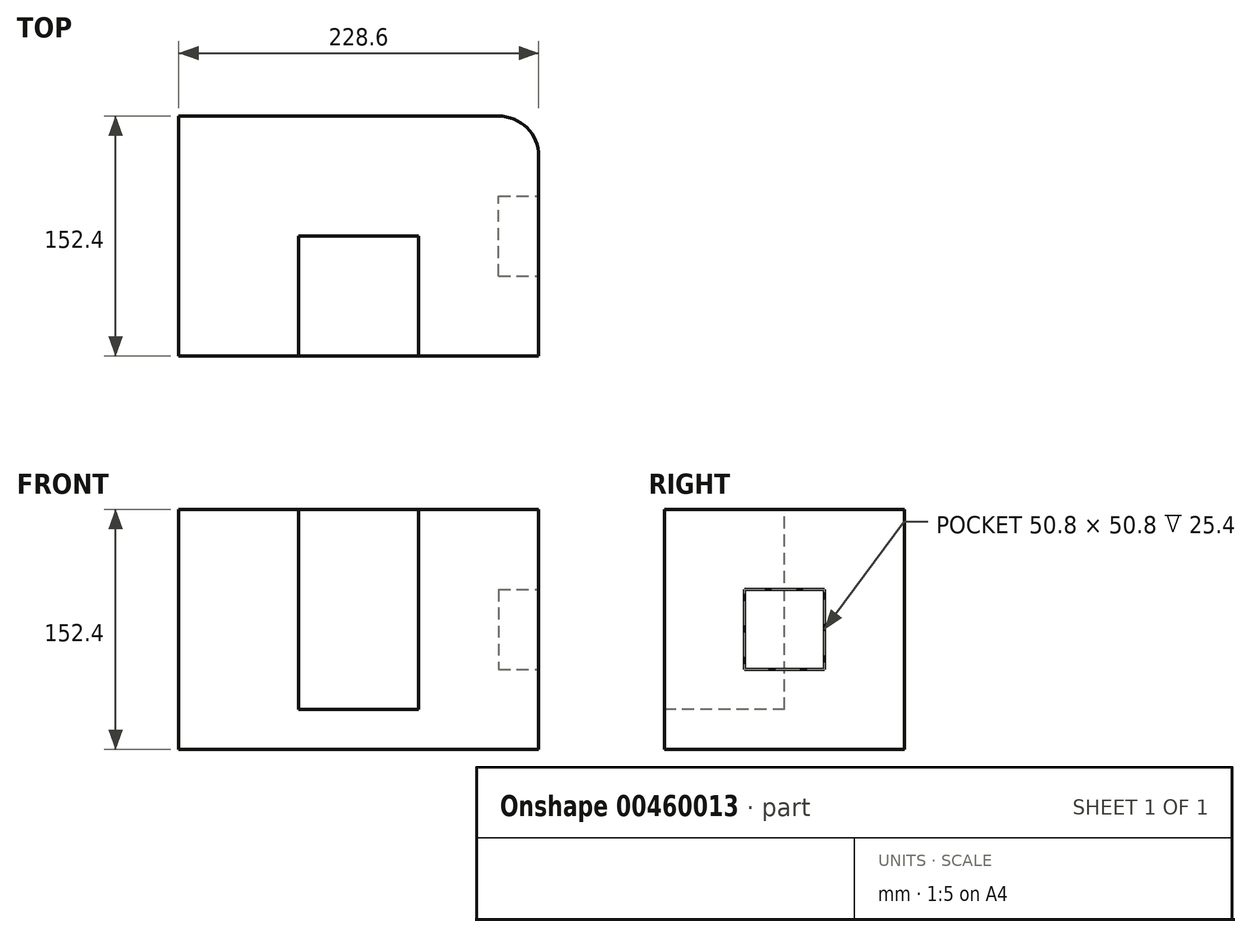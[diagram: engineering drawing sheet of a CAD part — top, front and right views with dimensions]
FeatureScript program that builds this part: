
annotation { "Feature Type Name" : "Feature", "Feature Type Description" : "" }
export const myFeature = defineFeature(function(context is Context, id is Id, definition is map)
    precondition{}
    {
        {
            var Q0;
            Q0=qCreatedBy(makeId("Front.planeOp"),FACE);
            var sketch = newSketch(context, id + "F0", { "sketchPlane" : qUnion([Q0])});
            skLineSegment(sketch, "E0", {"start": v(-151.97, 0) * mm, "end": v(-151.97, 152.4) * mm});
            skLineSegment(sketch, "E1", {"start": v(76.63, 152.4) * mm, "end": v(-151.97, 152.4) * mm});
            skLineSegment(sketch, "E2", {"start": v(76.63, 152.4) * mm, "end": v(76.63, 0) * mm});
            skLineSegment(sketch, "E3", {"start": v(-151.97, 0) * mm, "end": v(76.63, 0) * mm});
            skSolve(sketch);
        }
        {
            var Q0;
            Q0 = qSketchRegion(id + "F0", true);
            extrude(context, id + "F1", {"entities" : qUnion([Q0]), "depth" : 152.4 * mm});
        }
        {
            var Q0;
            Q0=makeQuery(id+"F1.opExtrude","CAP_FACE",FACE,{"disambiguationData":[OSD([sQuery(id+"F0.wireOp",EDGE,"E0"),sQuery(id+"F0.wireOp",EDGE,"E1"),sQuery(id+"F0.wireOp",EDGE,"E2"),sQuery(id+"F0.wireOp",EDGE,"E3")])],"isStart":false});
            var sketch = newSketch(context, id + "F2", { "sketchPlane" : qUnion([Q0])});
            skLineSegment(sketch, "E4.bottom", {"start": v(-151.97, 152.4) * mm, "end": v(-75.77, 152.4) * mm});
            skLineSegment(sketch, "E4.top", {"start": v(-151.97, 152.4) * mm, "end": v(-75.77, 152.4) * mm});
            skLineSegment(sketch, "E4.left", {"start": v(-151.97, 152.4) * mm, "end": v(-151.97, 152.4) * mm});
            skLineSegment(sketch, "E4.right", {"start": v(-75.77, 152.4) * mm, "end": v(-75.77, 152.4) * mm});
            skLineSegment(sketch, "E5.bottom", {"start": v(-75.77, 25.4) * mm, "end": v(0.43, 25.4) * mm});
            skLineSegment(sketch, "E5.top", {"start": v(-75.77, 152.4) * mm, "end": v(0.43, 152.4) * mm});
            skLineSegment(sketch, "E5.left", {"start": v(-75.77, 25.4) * mm, "end": v(-75.77, 152.4) * mm});
            skLineSegment(sketch, "E5.right", {"start": v(0.43, 25.4) * mm, "end": v(0.43, 152.4) * mm});
            skSolve(sketch);
        }
        {
            var Q0;
            Q0 = qSketchRegion(id + "F2", true);
            extrude(context, id + "F3", {"entities" : qUnion([Q0]), "operationType" : NewBodyOperationType.REMOVE, "oppositeDirection" : true, "depth" : 76.2 * mm});
        }
        {
            var Q0;
            Q0=makeQuery(id+"F1.opExtrude","SWEPT_FACE",FACE,{"disambiguationData":[OSD([sQuery(id+"F0.wireOp",EDGE,"E2")])]});
            var sketch = newSketch(context, id + "F4", { "sketchPlane" : qUnion([Q0])});
            skLineSegment(sketch, "E6.bottom", {"start": v(-101.6, 101.6) * mm, "end": v(-50.8, 101.6) * mm});
            skLineSegment(sketch, "E6.top", {"start": v(-101.6, 50.8) * mm, "end": v(-50.8, 50.8) * mm});
            skLineSegment(sketch, "E6.left", {"start": v(-101.6, 101.6) * mm, "end": v(-101.6, 50.8) * mm});
            skLineSegment(sketch, "E6.right", {"start": v(-50.8, 101.6) * mm, "end": v(-50.8, 50.8) * mm});
            skSolve(sketch);
        }
        {
            var Q0;
            Q0 = qSketchRegion(id + "F4", true);
            extrude(context, id + "F5", {"entities" : qUnion([Q0]), "operationType" : NewBodyOperationType.REMOVE, "oppositeDirection" : true, "depth" : 25.4 * mm});
        }
        {
            var Q0;
            Q0=makeQuery(id+"F1.opExtrude","CAP_EDGE",EDGE,{"disambiguationData":[OSD([sQuery(id+"F0.wireOp",EDGE,"E2")])],"isStart":true});
            fillet(context, id + "F6", {"entities" : qUnion([Q0]), "radius" : 25.4 * mm, "tangentPropagation" : true, "allowEdgeOverflow" : false});
        }
    });
